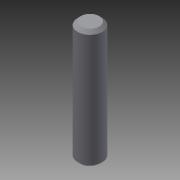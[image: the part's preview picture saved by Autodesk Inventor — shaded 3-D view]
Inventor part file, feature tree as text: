
AUTODESK INVENTOR PART (.ipt)
format: ipt  version: 2014 SP2 (Build 180246200, 246)  size: 88,064 bytes
history: native  units: in
note: dims shown in document units (in); Inventor stores cm internally (conversion verified against a paired STEP export)
features: other x7, revolve x1, sketch x1
ambient origin geometry x8: Origin, YZ Plane, XZ Plane, XY Plane, X Axis, Y Axis, Z Axis, Center Point
bodies: Solid1 (feature_tree)
feature tree (9):
  revolve  "Revolution1"  [1 undecoded]
  other  "to_a_XY"
  other  "to_a_YZ"
  other  "to_a_ZX"
  other  "to_a_X"
  other  "to_a_Y"
  other  "to_a_Z"
  other  "to_a_Center"
  sketch  "Sketch_1"  dims[d0=360.0deg]
note: 1 required parameter value undecoded (feature->parameter linkage not recoverable at this tier; creation-order binding heuristic only, values carry confidence <= 0.55)
